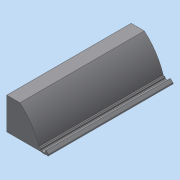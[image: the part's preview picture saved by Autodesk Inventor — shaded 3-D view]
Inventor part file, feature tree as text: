
AUTODESK INVENTOR PART (.ipt)
format: ipt  version: 2020 (Build 240168000, 168)  size: 143,360 bytes
history: native  units: mm
features: other x1, sweep x1, fillet x1, sketch x1
ambient origin geometry x8: Origin, YZ Plane, XZ Plane, XY Plane, X Axis, Y Axis, Z Axis, Center Point
bodies: Body1 (feature_tree)
feature tree (4):
  other  "實體1"
  sweep  "掃掠1"
  fillet  "圓角1"  Radius=1.0mm
  sketch  "草圖3"
